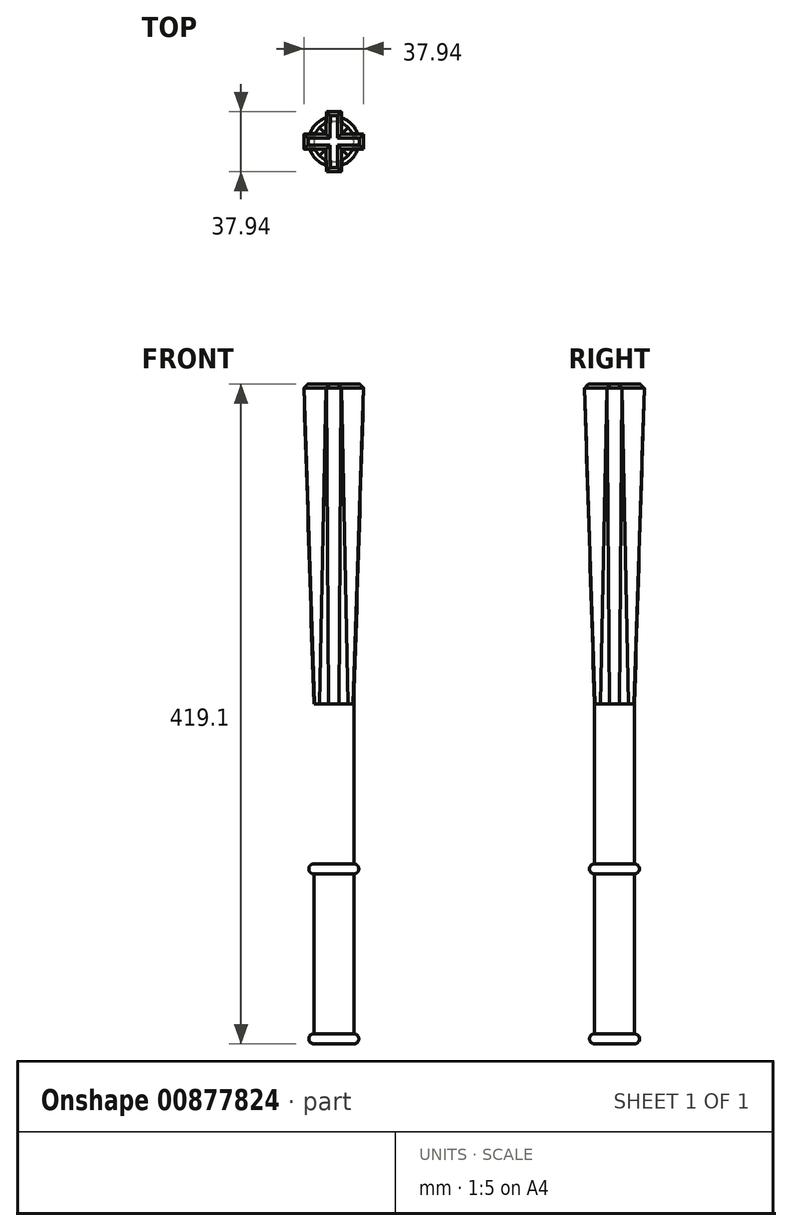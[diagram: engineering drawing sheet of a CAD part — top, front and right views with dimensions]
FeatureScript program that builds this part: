
annotation { "Feature Type Name" : "Feature", "Feature Type Description" : "" }
export const myFeature = defineFeature(function(context is Context, id is Id, definition is map)
    precondition{}
    {
        {
            var Q0;
            Q0=qCreatedBy(makeId("Top.planeOp"),FACE);
            var sketch = newSketch(context, id + "F0", { "sketchPlane" : qUnion([Q0])});
            skCircle(sketch, "E0", {"center": v(0, 0) * mm, "radius": 12.7 * mm});
            skSolve(sketch);
        }
        {
            var Q0;
            Q0=makeQuery(id+"F0.imprint","IMPRINT",FACE,{"disambiguationData":[TD([[makeQuery(id+"F0.imprint","IMPRINT",EDGE,{"derivedFrom":sQuery(id+"F0.wireOp",EDGE,"E0")}),1.0]])]});
            cPlane(context, id + "F1", {"entities" : qUnion([Q0]), "cplaneType" : CPlaneType.OFFSET, "offset" : 203.2 * mm, "width" : 152.4 * mm, "height" : 152.4 * mm});
        }
        {
            var Q0;
            Q0=qCreatedBy(id+"F1.planeOp",FACE);
            var sketch = newSketch(context, id + "F2", { "sketchPlane" : qUnion([Q0])});
            skLineSegment(sketch, "E1.0", {"start": v(4.76, 4.76) * mm, "end": v(4.76, 19.05) * mm});
            skLineSegment(sketch, "E2.0", {"start": v(-4.76, 4.76) * mm, "end": v(-4.76, 19.05) * mm});
            skLineSegment(sketch, "E3.0", {"start": v(19.05, 4.76) * mm, "end": v(4.76, 4.76) * mm});
            skLineSegment(sketch, "E4.0", {"start": v(19.05, -4.76) * mm, "end": v(4.76, -4.76) * mm});
            skLineSegment(sketch, "E5.0", {"start": v(4.76, -19.05) * mm, "end": v(4.76, -4.76) * mm});
            skLineSegment(sketch, "E6.0", {"start": v(-4.76, -19.05) * mm, "end": v(-4.76, -4.76) * mm});
            skLineSegment(sketch, "E7", {"start": v(-4.76, -19.05) * mm, "end": v(4.76, -19.05) * mm});
            skLineSegment(sketch, "E8", {"start": v(19.05, -4.76) * mm, "end": v(19.05, 4.76) * mm});
            skLineSegment(sketch, "E9", {"start": v(-19.05, -4.76) * mm, "end": v(-19.05, 4.76) * mm});
            skLineSegment(sketch, "E10", {"start": v(-4.76, 19.05) * mm, "end": v(4.76, 19.05) * mm});
            skLineSegment(sketch, "E11.trimOffspring", {"start": v(-4.76, 4.76) * mm, "end": v(-19.05, 4.76) * mm});
            skLineSegment(sketch, "E12.trimOffspring", {"start": v(-4.76, -4.76) * mm, "end": v(-19.05, -4.76) * mm});
            skSolve(sketch);
        }
        {
            var Q0;
            Q0=makeQuery(id+"F2.imprint","IMPRINT",FACE,{"disambiguationData":[TD([[makeQuery(id+"F2.imprint","IMPRINT",EDGE,{"derivedFrom":sQuery(id+"F2.wireOp",EDGE,"E1.0")}),1.0]])]});
            var Q1;
            Q1=makeQuery(id+"F0.imprint","IMPRINT",FACE,{"disambiguationData":[TD([[makeQuery(id+"F0.imprint","IMPRINT",EDGE,{"derivedFrom":sQuery(id+"F0.wireOp",EDGE,"E0")}),1.0]])]});
            loft(context, id + "F3", {"sheetProfilesArray" : [{ "sheetProfileEntities" : qUnion([Q0]) }, { "sheetProfileEntities" : qUnion([Q1]) }]});
        }
        {
            var Q0;
            Q0=makeQuery(id+"F3.opLoft","CAP_FACE",FACE,{"disambiguationData":[OSD([makeQuery(id+"F0.imprint","IMPRINT",FACE,{"disambiguationData":[TD([[makeQuery(id+"F0.imprint","IMPRINT",EDGE,{"derivedFrom":sQuery(id+"F0.wireOp",EDGE,"E0")}),1.0]])]})])],"isStart":true});
            extrude(context, id + "F4", {"entities" : qUnion([Q0]), "operationType" : NewBodyOperationType.ADD, "depth" : 101.6 * mm, "offsetDistance" : 25.4 * mm});
        }
        {
            var Q0;
            Q0=makeQuery(id+"F3.opLoft","CAP_FACE",FACE,{"disambiguationData":[OSD([makeQuery(id+"F2.imprint","IMPRINT",FACE,{"disambiguationData":[TD([[makeQuery(id+"F2.imprint","IMPRINT",EDGE,{"derivedFrom":sQuery(id+"F2.wireOp",EDGE,"E1.0")}),1.0]])]})])],"isStart":true});
            chamfer(context, id + "F5", {"entities" : qUnion([Q0]), "width" : 2.54 * mm, "tangentPropagation" : true});
        }
        {
            var Q0;
            Q0=makeQuery(id+"F4.opExtrude","CAP_FACE",FACE,{"disambiguationData":[OSD([makeQuery(id+"F0.imprint","IMPRINT",FACE,{"disambiguationData":[TD([[makeQuery(id+"F0.imprint","IMPRINT",EDGE,{"derivedFrom":sQuery(id+"F0.wireOp",EDGE,"E0")}),1.0]])]})])],"isStart":false});
            var sketch = newSketch(context, id + "F6", { "sketchPlane" : qUnion([Q0])});
            skCircle(sketch, "E13", {"center": v(0, 0) * mm, "radius": 15.88 * mm});
            skSolve(sketch);
        }
        {
            var Q0;
            Q0 = qSketchRegion(id + "F6", true);
            extrude(context, id + "F7", {"entities" : qUnion([Q0]), "operationType" : NewBodyOperationType.ADD, "depth" : 6.35 * mm, "offsetDistance" : 25.4 * mm});
        }
        {
            var Q0;
            Q0=makeQuery(id+"F7.opExtrude","CAP_EDGE",EDGE,{"disambiguationData":[OSD([sQuery(id+"F6.wireOp",EDGE,"E13")])],"isStart":true});
            var Q1;
            Q1=makeQuery(id+"F7.opExtrude","CAP_EDGE",EDGE,{"disambiguationData":[OSD([sQuery(id+"F6.wireOp",EDGE,"E13")])],"isStart":false});
            fillet(context, id + "F8", {"entities" : qUnion([Q0, Q1]), "radius" : 3.17 * mm, "tangentPropagation" : true, "allowEdgeOverflow" : false});
        }
        {
            var Q0;
            Q0=makeQuery(id+"F7.opExtrude","CAP_FACE",FACE,{"disambiguationData":[OSD([sQuery(id+"F6.wireOp",EDGE,"E13")])],"isStart":false});
            extrude(context, id + "F9", {"entities" : qUnion([Q0]), "operationType" : NewBodyOperationType.ADD, "depth" : 101.6 * mm, "offsetDistance" : 25.4 * mm});
        }
        {
            var Q0;
            Q0=makeQuery(id+"F9.opExtrude","CAP_FACE",FACE,{"disambiguationData":[OSD([sQuery(id+"F6.wireOp",EDGE,"E13")])],"isStart":false});
            var sketch = newSketch(context, id + "F10", { "sketchPlane" : qUnion([Q0])});
            skCircle(sketch, "E14", {"center": v(0, 0) * mm, "radius": 15.88 * mm});
            skSolve(sketch);
        }
        {
            var Q0;
            Q0 = qSketchRegion(id + "F10", true);
            extrude(context, id + "F11", {"entities" : qUnion([Q0]), "operationType" : NewBodyOperationType.ADD, "depth" : 6.35 * mm, "offsetDistance" : 25.4 * mm});
        }
        {
            var Q0;
            Q0=makeQuery(id+"F11.opExtrude","CAP_EDGE",EDGE,{"disambiguationData":[OSD([sQuery(id+"F10.wireOp",EDGE,"E14")])],"isStart":true});
            var Q1;
            Q1=makeQuery(id+"F11.opExtrude","CAP_EDGE",EDGE,{"disambiguationData":[OSD([sQuery(id+"F10.wireOp",EDGE,"E14")])],"isStart":false});
            fillet(context, id + "F12", {"entities" : qUnion([Q0, Q1]), "radius" : 3.17 * mm, "tangentPropagation" : true, "allowEdgeOverflow" : false});
        }
    });
